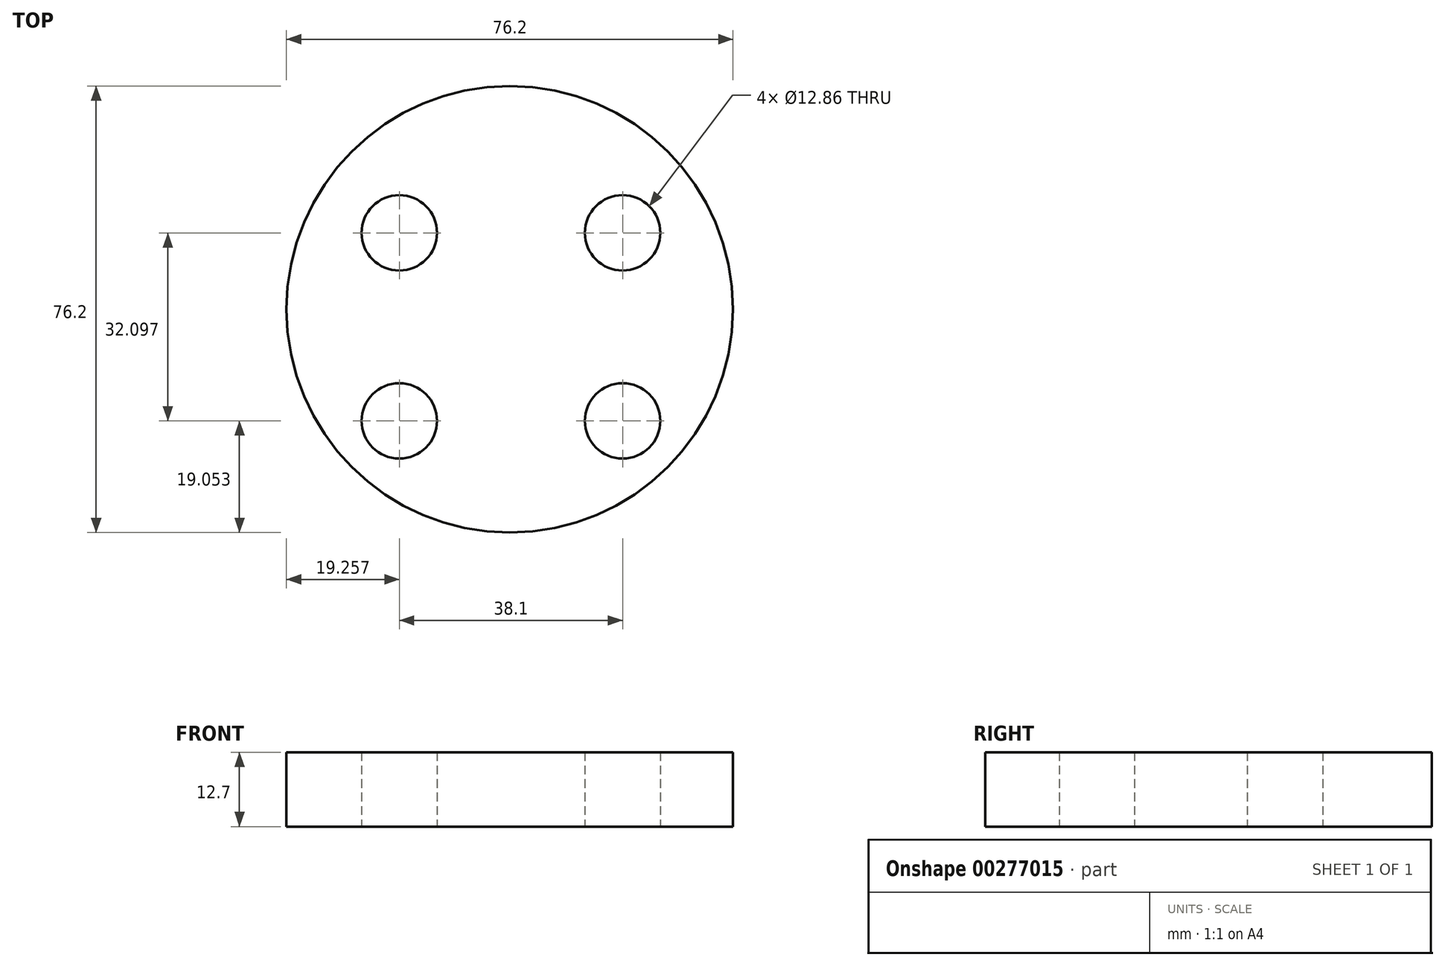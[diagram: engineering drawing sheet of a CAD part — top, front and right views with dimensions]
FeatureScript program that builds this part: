
annotation { "Feature Type Name" : "Feature", "Feature Type Description" : "" }
export const myFeature = defineFeature(function(context is Context, id is Id, definition is map)
    precondition{}
    {
        {
            var Q0;
            Q0=qCreatedBy(makeId("Top.planeOp"),FACE);
            var sketch = newSketch(context, id + "F0", { "sketchPlane" : qUnion([Q0])});
            skCircle(sketch, "E0", {"center": v(-34.77, -13.05) * mm, "radius": 38.1 * mm});
            skCircle(sketch, "E1", {"center": v(-53.61, 0) * mm, "radius": 6.43 * mm});
            skCircle(sketch, "E2.2.0", {"center": v(-15.51, 0) * mm, "radius": 6.43 * mm});
            skPoint(sketch, "E2.center", {"position": v(-34.56, 0) * mm});
            skLineSegment(sketch, "E2.anchor1", {"start": v(-34.56, 0) * mm, "end": v(-53.61, 0) * mm, "construction": true});
            skLineSegment(sketch, "E2.anchor2", {"start": v(-34.56, 0) * mm, "end": v(-15.51, 0) * mm, "construction": true});
            skCircle(sketch, "E3", {"center": v(-53.61, -32.1) * mm, "radius": 6.43 * mm});
            skCircle(sketch, "E4.2.0", {"center": v(-15.51, -32.1) * mm, "radius": 6.43 * mm});
            skPoint(sketch, "E4.center", {"position": v(-34.56, -32.1) * mm});
            skLineSegment(sketch, "E4.anchor1", {"start": v(-34.56, -32.1) * mm, "end": v(-53.61, -32.1) * mm, "construction": true});
            skLineSegment(sketch, "E4.anchor2", {"start": v(-34.56, -32.1) * mm, "end": v(-15.51, -32.1) * mm, "construction": true});
            skSolve(sketch);
        }
        {
            var Q0;
            Q0=makeQuery(id+"F0.imprint","IMPRINT",FACE,{"disambiguationData":[TD([[makeQuery(id+"F0.imprint","IMPRINT",EDGE,{"derivedFrom":sQuery(id+"F0.wireOp",EDGE,"E0")}),1.0]])]});
            extrude(context, id + "F1", {"entities" : qUnion([Q0]), "depth" : 12.7 * mm});
        }
    });
